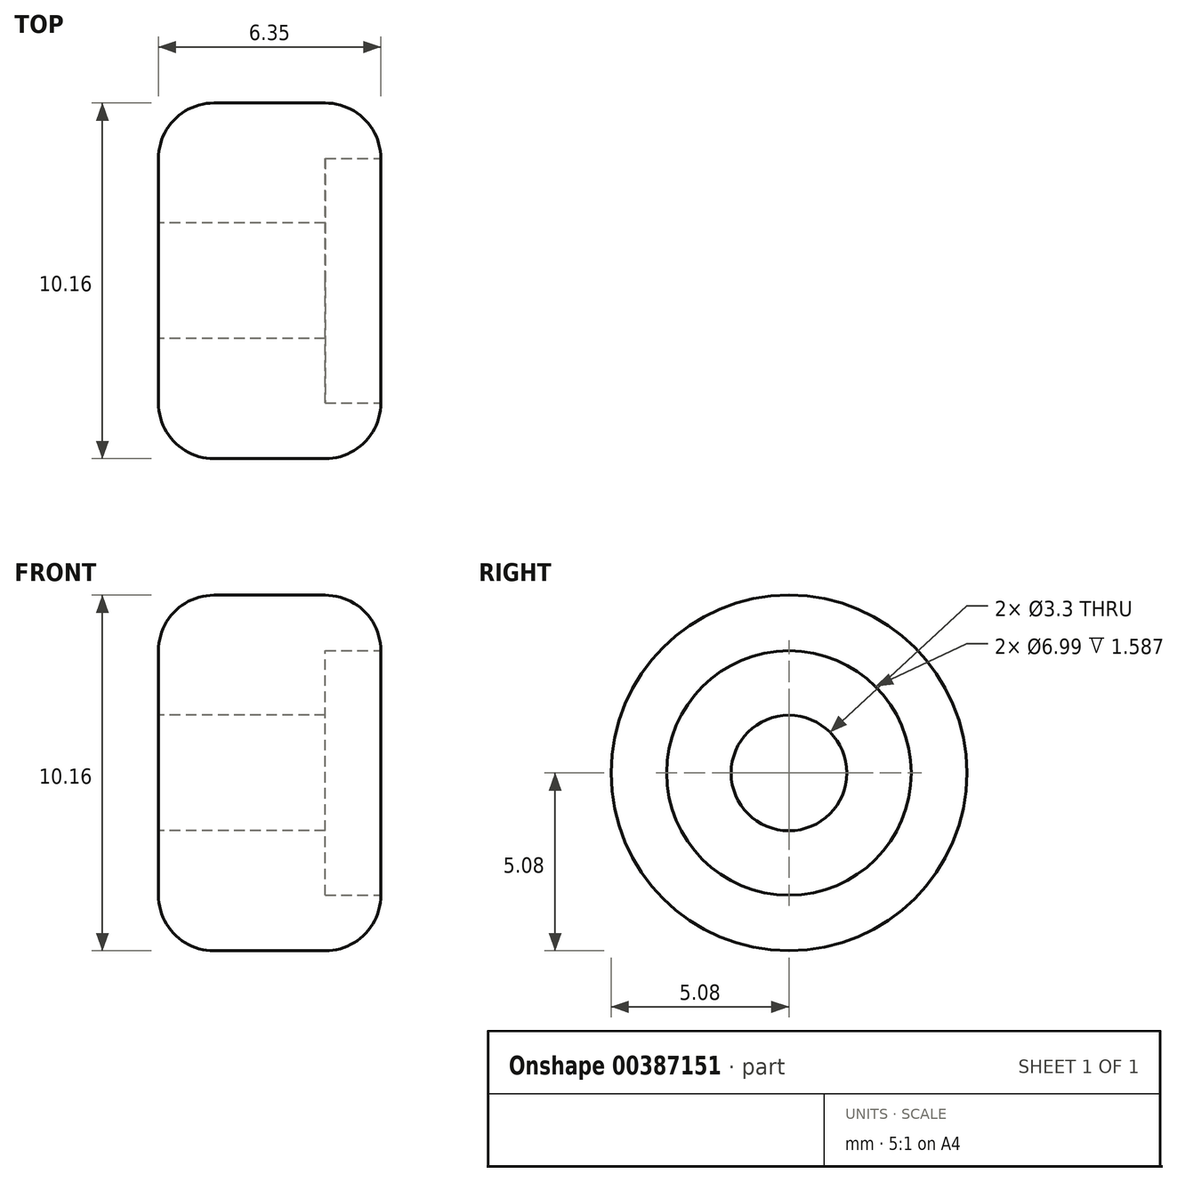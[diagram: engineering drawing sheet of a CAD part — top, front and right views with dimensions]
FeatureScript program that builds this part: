
annotation { "Feature Type Name" : "Feature", "Feature Type Description" : "" }
export const myFeature = defineFeature(function(context is Context, id is Id, definition is map)
    precondition{}
    {
        {
            var Q0;
            Q0=qCreatedBy(makeId("Right.planeOp"),FACE);
            var sketch = newSketch(context, id + "F0", { "sketchPlane" : qUnion([Q0])});
            skCircle(sketch, "E0", {"center": v(0, 0) * mm, "radius": 5.08 * mm});
            skCircle(sketch, "E1", {"center": v(0, 0) * mm, "radius": 1.65 * mm});
            skSolve(sketch);
        }
        {
            var Q0;
            Q0 = qSketchRegion(id + "F0", true);
            extrude(context, id + "F1", {"entities" : qUnion([Q0]), "depth" : 6.35 * mm});
        }
        {
            var Q0;
            Q0=makeQuery(id+"F1.opExtrude","CAP_EDGE",EDGE,{"disambiguationData":[OSD([sQuery(id+"F0.wireOp",EDGE,"E0")])],"isStart":false});
            var Q1;
            Q1=makeQuery(id+"F1.opExtrude","CAP_EDGE",EDGE,{"disambiguationData":[OSD([sQuery(id+"F0.wireOp",EDGE,"E0")])],"isStart":true});
            fillet(context, id + "F2", {"entities" : qUnion([Q0, Q1]), "radius" : 1.59 * mm, "tangentPropagation" : true, "allowEdgeOverflow" : false});
        }
        {
            var Q0;
            Q0=makeQuery(id+"F1.opExtrude","CAP_FACE",FACE,{"disambiguationData":[OSD([sQuery(id+"F0.wireOp",EDGE,"E0"),sQuery(id+"F0.wireOp",EDGE,"E1")])],"isStart":false});
            var sketch = newSketch(context, id + "F3", { "sketchPlane" : qUnion([Q0])});
            skCircle(sketch, "E2", {"center": v(0, 0) * mm, "radius": 1.65 * mm});
            skCircle(sketch, "E3", {"center": v(0, 0) * mm, "radius": 3.5 * mm});
            skSolve(sketch);
        }
        {
            var Q0;
            Q0 = qSketchRegion(id + "F3", true);
            extrude(context, id + "F4", {"entities" : qUnion([Q0]), "operationType" : NewBodyOperationType.REMOVE, "oppositeDirection" : true, "depth" : 1.59 * mm});
        }
    });
